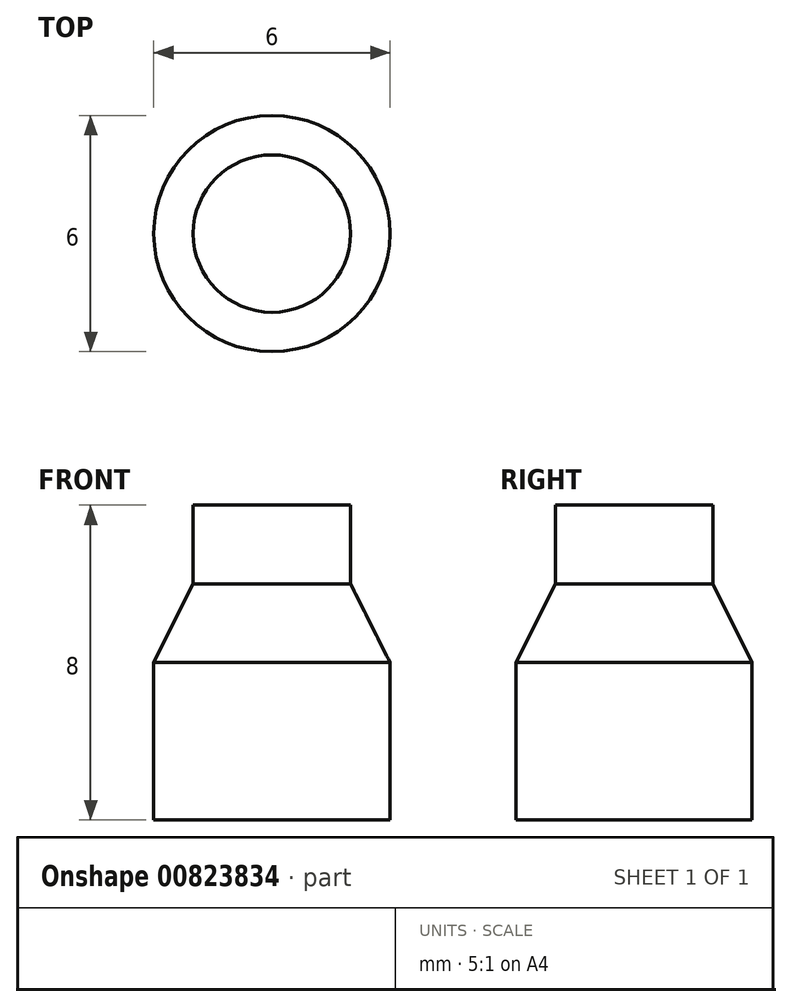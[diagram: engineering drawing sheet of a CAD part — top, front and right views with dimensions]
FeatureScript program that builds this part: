
annotation { "Feature Type Name" : "Feature", "Feature Type Description" : "" }
export const myFeature = defineFeature(function(context is Context, id is Id, definition is map)
    precondition{}
    {
        {
            var Q0;
            Q0=qCreatedBy(makeId("Front.planeOp"),FACE);
            var sketch = newSketch(context, id + "F0", { "sketchPlane" : qUnion([Q0])});
            skLineSegment(sketch, "E0", {"start": v(0, 0) * mm, "end": v(3, 0) * mm});
            skLineSegment(sketch, "E1", {"start": v(3, 0) * mm, "end": v(3, 4) * mm});
            skLineSegment(sketch, "E2", {"start": v(3, 4) * mm, "end": v(2, 6) * mm});
            skLineSegment(sketch, "E3", {"start": v(2, 6) * mm, "end": v(2, 8) * mm});
            skLineSegment(sketch, "E4", {"start": v(2, 8) * mm, "end": v(0, 8) * mm});
            skLineSegment(sketch, "E5", {"start": v(0, 8) * mm, "end": v(0, 0) * mm});
            skSolve(sketch);
        }
        {
            var Q0;
            Q0=makeQuery(id+"F0.imprint","IMPRINT",FACE,{"disambiguationData":[TD([[makeQuery(id+"F0.imprint","IMPRINT",EDGE,{"derivedFrom":sQuery(id+"F0.wireOp",EDGE,"E0")}),1.0]])]});
            var Q1;
            Q1=sQuery(id+"F0.wireOp",EDGE,"E5");
            revolve(context, id + "F1", {"surfaceOperationType" : NewSurfaceOperationType.NEW, "entities" : qUnion([Q0]), "axis" : qUnion([Q1]), "revolveType" : RevolveType.FULL});
        }
    });
